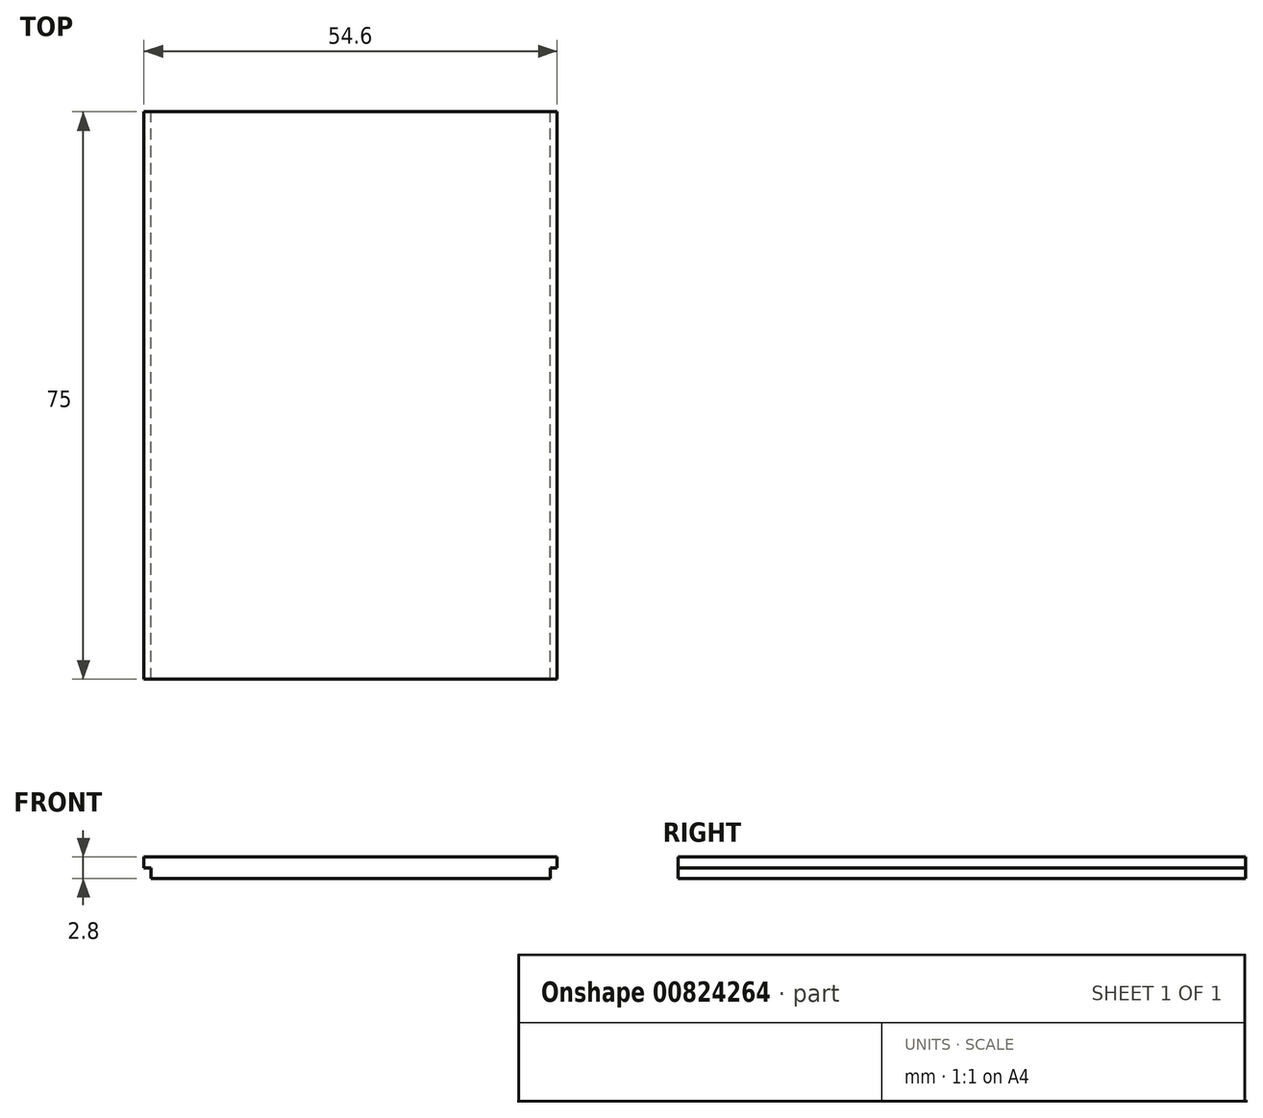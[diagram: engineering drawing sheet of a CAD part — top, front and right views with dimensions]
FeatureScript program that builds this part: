
annotation { "Feature Type Name" : "Feature", "Feature Type Description" : "" }
export const myFeature = defineFeature(function(context is Context, id is Id, definition is map)
    precondition{}
    {
        {
            var Q0;
            Q0=qCreatedBy(makeId("Front.planeOp"),FACE);
            var sketch = newSketch(context, id + "F0", { "sketchPlane" : qUnion([Q0])});
            skLineSegment(sketch, "E0.bottom", {"start": v(-26.4, 0) * mm, "end": v(26.4, 0) * mm});
            skLineSegment(sketch, "E0.top", {"start": v(-26.4, 2.8) * mm, "end": v(26.4, 2.8) * mm});
            skLineSegment(sketch, "E0.left", {"start": v(-26.4, 0) * mm, "end": v(-26.4, 1.4) * mm});
            skLineSegment(sketch, "E0.right", {"start": v(26.4, 0) * mm, "end": v(26.4, 1.4) * mm});
            skPoint(sketch, "E1", {"position": v(0, 0) * mm});
            skPoint(sketch, "E2.oppositeSnap0", {"position": v(26.4, 1.4) * mm});
            skLineSegment(sketch, "E2.bottom", {"start": v(26.4, 2.8) * mm, "end": v(27.3, 2.8) * mm});
            skLineSegment(sketch, "E2.top", {"start": v(26.4, 1.4) * mm, "end": v(27.3, 1.4) * mm});
            skLineSegment(sketch, "E2.right", {"start": v(27.3, 2.8) * mm, "end": v(27.3, 1.4) * mm});
            skLineSegment(sketch, "E3.bottom", {"start": v(27.3, 1.4) * mm, "end": v(27.3, 1.4) * mm});
            skLineSegment(sketch, "E3.top", {"start": v(27.3, 2.8) * mm, "end": v(27.3, 2.8) * mm});
            skLineSegment(sketch, "E3.left", {"start": v(27.3, 1.4) * mm, "end": v(27.3, 2.8) * mm});
            skLineSegment(sketch, "E3.right", {"start": v(27.3, 1.4) * mm, "end": v(27.3, 2.8) * mm});
            skPoint(sketch, "E4.oppositeSnap0", {"position": v(-26.4, 1.4) * mm});
            skLineSegment(sketch, "E4.bottom", {"start": v(-26.4, 2.8) * mm, "end": v(-27.3, 2.8) * mm});
            skLineSegment(sketch, "E4.top", {"start": v(-26.4, 1.4) * mm, "end": v(-27.3, 1.4) * mm});
            skLineSegment(sketch, "E4.right", {"start": v(-27.3, 2.8) * mm, "end": v(-27.3, 1.4) * mm});
            skSolve(sketch);
        }
        {
            var Q0;
            Q0 = qSketchRegion(id + "F0", true);
            extrude(context, id + "F1", {"entities" : qUnion([Q0]), "depth" : 75 * mm, "offsetDistance" : 25 * mm});
        }
    });
